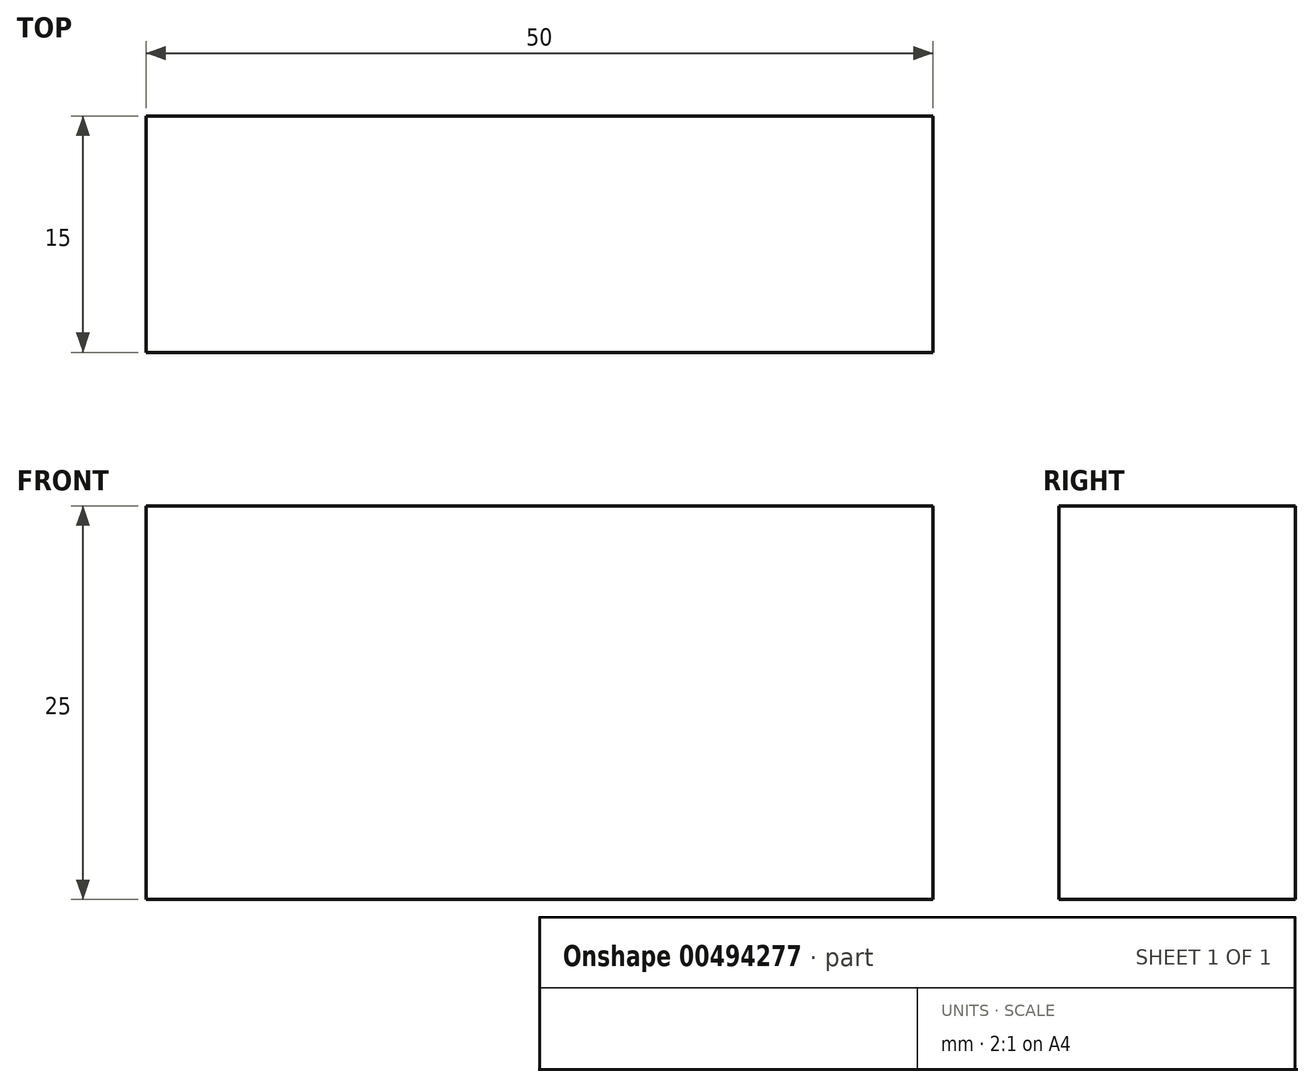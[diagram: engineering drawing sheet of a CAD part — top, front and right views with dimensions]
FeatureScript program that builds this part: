
annotation { "Feature Type Name" : "Feature", "Feature Type Description" : "" }
export const myFeature = defineFeature(function(context is Context, id is Id, definition is map)
    precondition{}
    {
        {
            var Q0;
            Q0=qCreatedBy(makeId("Top.planeOp"),FACE);
            var sketch = newSketch(context, id + "F0", { "sketchPlane" : qUnion([Q0])});
            skLineSegment(sketch, "E0.bottom", {"start": v(25, -7.5) * mm, "end": v(-25, -7.5) * mm});
            skLineSegment(sketch, "E0.top", {"start": v(25, 7.5) * mm, "end": v(-25, 7.5) * mm});
            skLineSegment(sketch, "E0.left", {"start": v(25, -7.5) * mm, "end": v(25, 7.5) * mm});
            skLineSegment(sketch, "E0.right", {"start": v(-25, -7.5) * mm, "end": v(-25, 7.5) * mm});
            skPoint(sketch, "E0.middle", {"position": v(0, 0) * mm});
            skSolve(sketch);
        }
        {
            var Q0;
            Q0=qSketchRegion(id+"F0",true);
            extrude(context, id + "F1", {"entities" : qUnion([Q0]), "depth" : 25 * mm});
        }
    });
